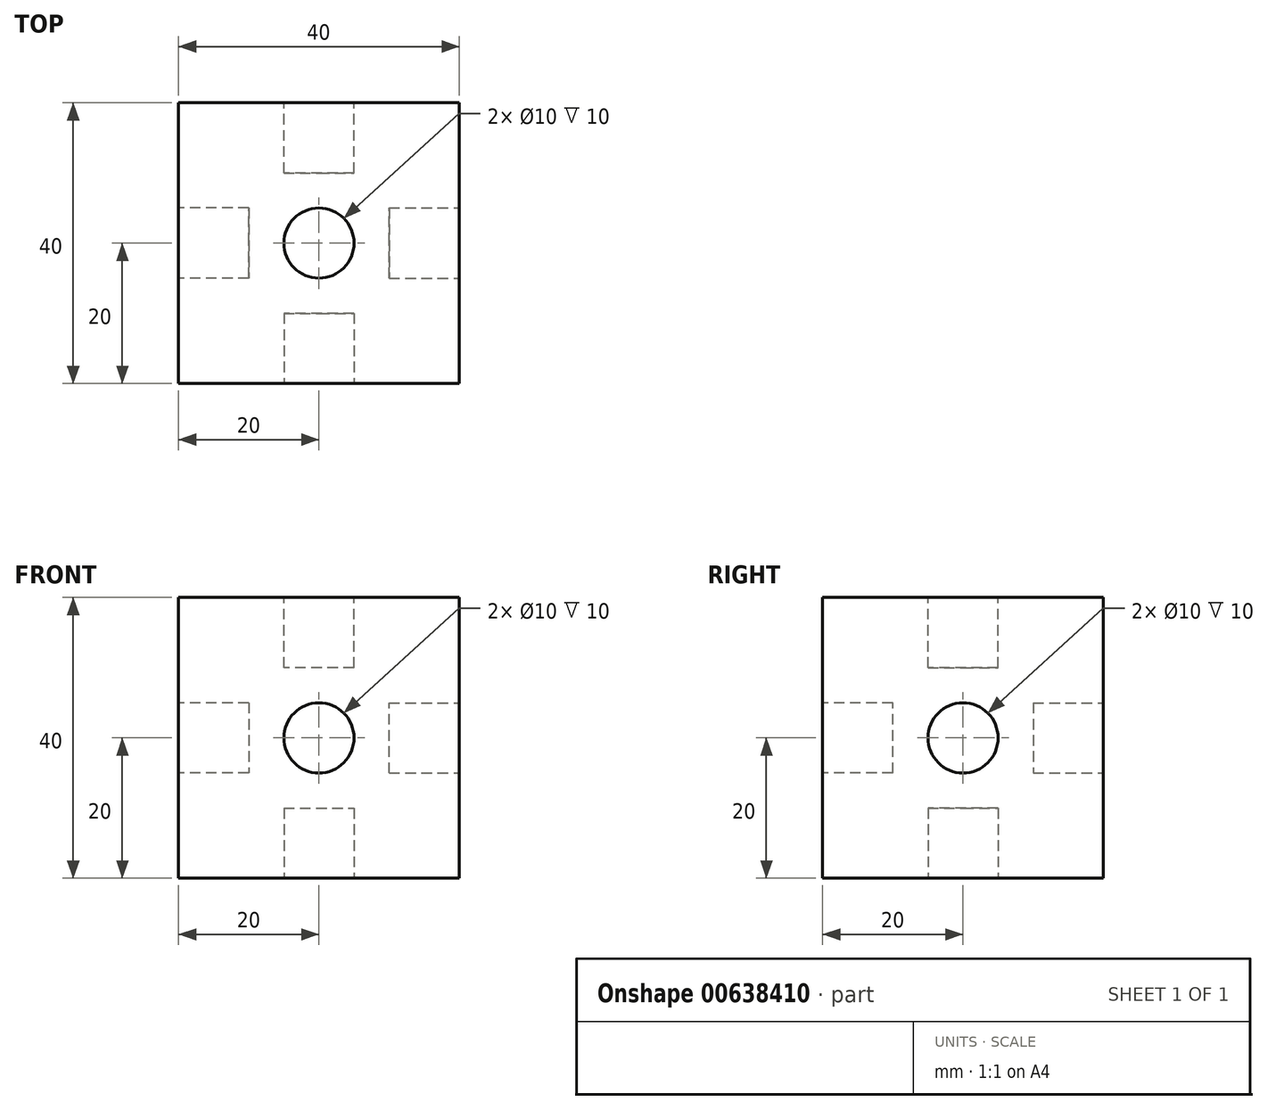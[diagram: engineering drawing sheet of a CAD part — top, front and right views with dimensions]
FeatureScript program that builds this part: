
annotation { "Feature Type Name" : "Feature", "Feature Type Description" : "" }
export const myFeature = defineFeature(function(context is Context, id is Id, definition is map)
    precondition{}
    {
        {
            var Q0;
            Q0=qCreatedBy(makeId("Top.planeOp"),FACE);
            var sketch = newSketch(context, id + "F0", { "sketchPlane" : qUnion([Q0])});
            skLineSegment(sketch, "E0", {"start": v(0, 0) * mm, "end": v(40, 0) * mm});
            skLineSegment(sketch, "E1", {"start": v(40, 0) * mm, "end": v(40, -40) * mm});
            skLineSegment(sketch, "E2", {"start": v(40, -40) * mm, "end": v(0, -40) * mm});
            skLineSegment(sketch, "E3", {"start": v(0, -40) * mm, "end": v(0, 0) * mm});
            skSolve(sketch);
        }
        {
            var Q0;
            Q0 = qSketchRegion(id + "F0", true);
            extrude(context, id + "F1", {"entities" : qUnion([Q0]), "depth" : 40 * mm, "offsetDistance" : 25 * mm});
        }
        {
            var Q0;
            Q0=makeQuery(id+"F1.opExtrude","CAP_FACE",FACE,{"disambiguationData":[OSD([sQuery(id+"F0.wireOp",EDGE,"E0"),sQuery(id+"F0.wireOp",EDGE,"E1"),sQuery(id+"F0.wireOp",EDGE,"E2"),sQuery(id+"F0.wireOp",EDGE,"E3")])],"isStart":false});
            var sketch = newSketch(context, id + "F2", { "sketchPlane" : qUnion([Q0])});
            skCircle(sketch, "E4", {"center": v(20, -20) * mm, "radius": 5 * mm});
            skSolve(sketch);
        }
        {
            var Q0;
            Q0=makeQuery(id+"F2.imprint","IMPRINT",FACE,{"disambiguationData":[TD([[makeQuery(id+"F2.imprint","IMPRINT",EDGE,{"derivedFrom":sQuery(id+"F2.wireOp",EDGE,"E4")}),1.0]])]});
            extrude(context, id + "F3", {"entities" : qUnion([Q0]), "operationType" : NewBodyOperationType.REMOVE, "oppositeDirection" : true, "depth" : 10 * mm, "offsetDistance" : 25 * mm});
        }
        {
            var Q0;
            Q0=makeQuery(id+"F1.opExtrude","SWEPT_FACE",FACE,{"disambiguationData":[OSD([sQuery(id+"F0.wireOp",EDGE,"E0")])]});
            var sketch = newSketch(context, id + "F4", { "sketchPlane" : qUnion([Q0])});
            skCircle(sketch, "E5", {"center": v(-20, 20) * mm, "radius": 5 * mm});
            skSolve(sketch);
        }
        {
            var Q0;
            Q0=makeQuery(id+"F4.imprint","IMPRINT",FACE,{"disambiguationData":[TD([[makeQuery(id+"F4.imprint","IMPRINT",EDGE,{"derivedFrom":sQuery(id+"F4.wireOp",EDGE,"E5")}),1.0]])]});
            extrude(context, id + "F5", {"entities" : qUnion([Q0]), "operationType" : NewBodyOperationType.REMOVE, "oppositeDirection" : true, "depth" : 10 * mm, "offsetDistance" : 25 * mm});
        }
        {
            var Q0;
            Q0=makeQuery(id+"F1.opExtrude","CAP_FACE",FACE,{"disambiguationData":[OSD([sQuery(id+"F0.wireOp",EDGE,"E0"),sQuery(id+"F0.wireOp",EDGE,"E1"),sQuery(id+"F0.wireOp",EDGE,"E2"),sQuery(id+"F0.wireOp",EDGE,"E3")])],"isStart":true});
            var sketch = newSketch(context, id + "F6", { "sketchPlane" : qUnion([Q0])});
            skCircle(sketch, "E6", {"center": v(20, 20) * mm, "radius": 5 * mm});
            skSolve(sketch);
        }
        {
            var Q0;
            Q0=makeQuery(id+"F6.imprint","IMPRINT",FACE,{"disambiguationData":[TD([[makeQuery(id+"F6.imprint","IMPRINT",EDGE,{"derivedFrom":sQuery(id+"F6.wireOp",EDGE,"E6")}),1.0]])]});
            extrude(context, id + "F7", {"entities" : qUnion([Q0]), "operationType" : NewBodyOperationType.REMOVE, "oppositeDirection" : true, "depth" : 10 * mm, "offsetDistance" : 25 * mm});
        }
        {
            var Q0;
            Q0=makeQuery(id+"F1.opExtrude","SWEPT_FACE",FACE,{"disambiguationData":[OSD([sQuery(id+"F0.wireOp",EDGE,"E2")])]});
            var sketch = newSketch(context, id + "F8", { "sketchPlane" : qUnion([Q0])});
            skCircle(sketch, "E7", {"center": v(20, 20) * mm, "radius": 5 * mm});
            skSolve(sketch);
        }
        {
            var Q0;
            Q0=makeQuery(id+"F8.imprint","IMPRINT",FACE,{"disambiguationData":[TD([[makeQuery(id+"F8.imprint","IMPRINT",EDGE,{"derivedFrom":sQuery(id+"F8.wireOp",EDGE,"E7")}),1.0]])]});
            extrude(context, id + "F9", {"entities" : qUnion([Q0]), "operationType" : NewBodyOperationType.REMOVE, "oppositeDirection" : true, "depth" : 10 * mm, "offsetDistance" : 25 * mm});
        }
        {
            var Q0;
            Q0=makeQuery(id+"F1.opExtrude","SWEPT_FACE",FACE,{"disambiguationData":[OSD([sQuery(id+"F0.wireOp",EDGE,"E1")])]});
            var sketch = newSketch(context, id + "F10", { "sketchPlane" : qUnion([Q0])});
            skCircle(sketch, "E8", {"center": v(-20, 20) * mm, "radius": 5 * mm});
            skSolve(sketch);
        }
        {
            var Q0;
            Q0=makeQuery(id+"F10.imprint","IMPRINT",FACE,{"disambiguationData":[TD([[makeQuery(id+"F10.imprint","IMPRINT",EDGE,{"derivedFrom":sQuery(id+"F10.wireOp",EDGE,"E8")}),1.0]])]});
            extrude(context, id + "F11", {"entities" : qUnion([Q0]), "operationType" : NewBodyOperationType.REMOVE, "oppositeDirection" : true, "depth" : 10 * mm, "offsetDistance" : 25 * mm});
        }
        {
            var Q0;
            Q0=makeQuery(id+"F1.opExtrude","SWEPT_FACE",FACE,{"disambiguationData":[OSD([sQuery(id+"F0.wireOp",EDGE,"E3")])]});
            var sketch = newSketch(context, id + "F12", { "sketchPlane" : qUnion([Q0])});
            skCircle(sketch, "E9", {"center": v(20, 20) * mm, "radius": 5 * mm});
            skSolve(sketch);
        }
        {
            var Q0;
            Q0=makeQuery(id+"F12.imprint","IMPRINT",FACE,{"disambiguationData":[TD([[makeQuery(id+"F12.imprint","IMPRINT",EDGE,{"derivedFrom":sQuery(id+"F12.wireOp",EDGE,"E9")}),1.0]])]});
            extrude(context, id + "F13", {"entities" : qUnion([Q0]), "operationType" : NewBodyOperationType.REMOVE, "oppositeDirection" : true, "depth" : 10 * mm, "offsetDistance" : 25 * mm});
        }
    });
